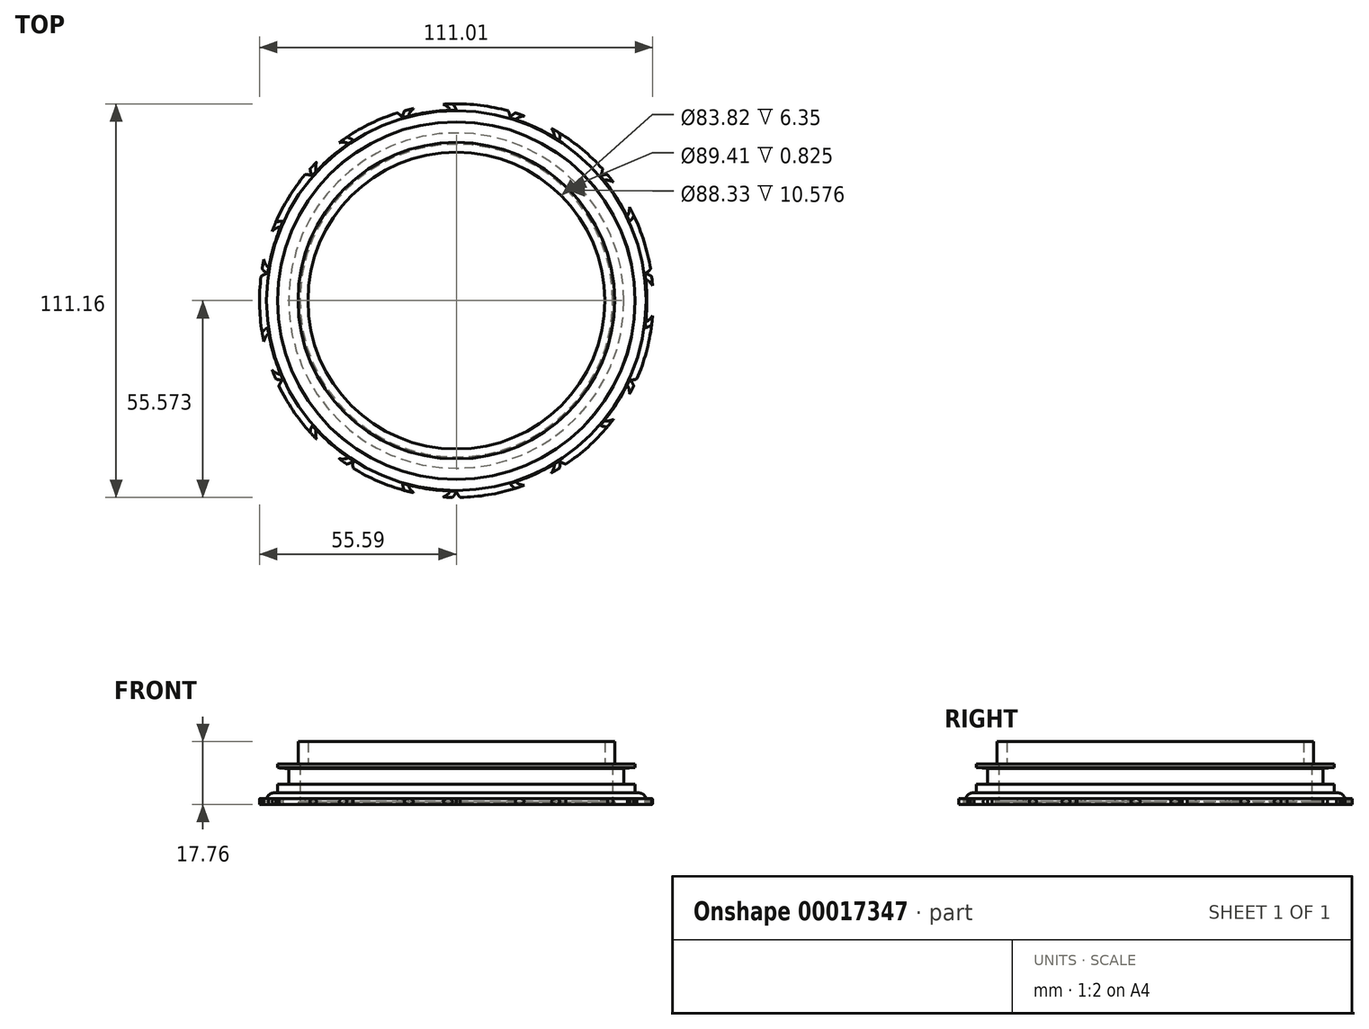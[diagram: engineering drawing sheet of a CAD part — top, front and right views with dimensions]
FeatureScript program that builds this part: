
annotation { "Feature Type Name" : "Feature", "Feature Type Description" : "" }
export const myFeature = defineFeature(function(context is Context, id is Id, definition is map)
    precondition{}
    {
        {
            var Q0;
            Q0=qCreatedBy(makeId("Top.planeOp"),FACE);
            var sketch = newSketch(context, id + "F0", { "sketchPlane" : qUnion([Q0])});
            skCircle(sketch, "E0", {"center": v(0, 0) * mm, "radius": 57.15 * mm, "construction": true});
            skLineSegment(sketch, "E1", {"start": v(0, 0) * mm, "end": v(0, 57.15) * mm, "construction": true});
            skCircle(sketch, "E2", {"center": v(0, 3.34) * mm, "radius": 53.8 * mm});
            skCircle(sketch, "E3", {"center": v(0, 3.34) * mm, "radius": 3.34 * mm, "construction": true});
            skLineSegment(sketch, "E4", {"start": v(0, 3.34) * mm, "end": v(-29.1, 48.6) * mm, "construction": true});
            skLineSegment(sketch, "E5", {"start": v(0, 57.15) * mm, "end": v(-29.1, 48.6) * mm, "construction": true});
            skLineSegment(sketch, "E6", {"start": v(-14.55, 52.88) * mm, "end": v(-29.1, 48.6) * mm, "construction": true});
            skLineSegment(sketch, "E7", {"start": v(-14.02, 24.18) * mm, "end": v(-21.82, 50.74) * mm, "construction": true});
            skCircle(sketch, "E8", {"center": v(-14.55, 52.88) * mm, "radius": 7.58 * mm, "construction": true});
            skLineSegment(sketch, "E9", {"start": v(-15.16, 54.97) * mm, "end": v(-16.68, 60.15) * mm, "construction": true});
            skEllipticalArc(sketch, "E10", {});
            skPoint(sketch, "E11", {"position": v(-15.16, 54.97) * mm});
            skLineSegment(sketch, "E12", {"start": v(-15.16, 54.97) * mm, "end": v(0, 54.97) * mm, "construction": true});
            skPoint(sketch, "E13", {"position": v(-7.58, 54.97) * mm});
            skCircle(sketch, "E14", {"center": v(0, 54.97) * mm, "radius": 7.58 * mm, "construction": true});
            skPoint(sketch, "E15", {"position": v(0, 62.55) * mm});
            skEllipticalArc(sketch, "E16", {});
            skCircle(sketch, "E17", {"center": v(0, 3.34) * mm, "radius": 44.7 * mm});
            skEllipticalArc(sketch, "E18.trimOffspring", {});
            skEllipticalArc(sketch, "E19.trimOffspring", {});
            skLineSegment(sketch, "E20", {"start": v(0, 3.34) * mm, "end": v(-8.33, 61.3) * mm, "construction": true});
            skCircle(sketch, "E21", {"center": v(0, 3.34) * mm, "radius": 55.59 * mm});
            skCircle(sketch, "E22", {"center": v(0, 3.34) * mm, "radius": 127 * mm});
            skLineSegment(sketch, "E23", {"start": v(0, 3.34) * mm, "end": v(-127, 3.34) * mm, "construction": true});
            skLineSegment(sketch, "E24", {"start": v(-53.8, 3.34) * mm, "end": v(-55.59, 3.34) * mm, "construction": true});
            skFitSpline(sketch, "E25.0", {"points": [v(-14.18, 56.14) * mm, v(-14.4, 54.97) * mm, v(-14.18, 53.8) * mm, v(-13.58, 52.8) * mm, v(-12.83, 52) * mm, v(-11.9, 51.22) * mm, v(-10.42, 50.32) * mm, v(-8.6, 49.57) * mm, v(-6.94, 49.07) * mm, v(-5.2, 48.66) * mm, v(-3.36, 48.38) * mm, v(-1.45, 48.24) * mm, v(0, 48.2) * mm, v(1.45, 48.24) * mm, v(3.36, 48.38) * mm, v(5.2, 48.66) * mm, v(6.94, 49.07) * mm, v(8.6, 49.57) * mm, v(10.42, 50.32) * mm, v(11.9, 51.22) * mm, v(12.83, 52) * mm, v(13.58, 52.8) * mm, v(14.18, 53.8) * mm, v(14.4, 54.97) * mm, v(14.18, 56.14) * mm, v(13.58, 57.14) * mm, v(12.83, 57.94) * mm, v(11.9, 58.72) * mm, v(10.42, 59.62) * mm, v(8.6, 60.37) * mm, v(6.94, 60.87) * mm, v(5.2, 61.28) * mm, v(3.36, 61.56) * mm, v(1.45, 61.7) * mm, v(0, 61.74) * mm, v(-1.45, 61.7) * mm, v(-3.36, 61.56) * mm, v(-5.2, 61.28) * mm, v(-6.94, 60.87) * mm, v(-8.6, 60.37) * mm, v(-10.42, 59.62) * mm, v(-11.9, 58.72) * mm, v(-12.83, 57.94) * mm, v(-13.58, 57.14) * mm, v(-14.18, 56.14) * mm, v(-14.4, 54.97) * mm, v(-14.18, 53.8) * mm]});
            skFitSpline(sketch, "E25.1", {"points": [v(-0.6, 55.75) * mm, v(-0.72, 56.94) * mm, v(-1.27, 58) * mm, v(-2.13, 58.8) * mm, v(-3.07, 59.34) * mm, v(-4.19, 59.83) * mm, v(-5.86, 60.28) * mm, v(-7.82, 60.48) * mm, v(-9.55, 60.5) * mm, v(-11.33, 60.4) * mm, v(-13.18, 60.15) * mm, v(-15.05, 59.75) * mm, v(-16.45, 59.37) * mm, v(-17.84, 58.93) * mm, v(-19.63, 58.25) * mm, v(-21.32, 57.47) * mm, v(-22.87, 56.58) * mm, v(-24.31, 55.64) * mm, v(-25.85, 54.4) * mm, v(-27.02, 53.13) * mm, v(-27.7, 52.12) * mm, v(-28.19, 51.14) * mm, v(-28.48, 50) * mm, v(-28.37, 48.82) * mm, v(-27.82, 47.76) * mm, v(-26.96, 46.97) * mm, v(-26.02, 46.41) * mm, v(-24.9, 45.93) * mm, v(-23.23, 45.48) * mm, v(-21.27, 45.27) * mm, v(-19.54, 45.26) * mm, v(-17.76, 45.36) * mm, v(-15.91, 45.61) * mm, v(-14.04, 46.01) * mm, v(-12.64, 46.39) * mm, v(-11.25, 46.83) * mm, v(-9.47, 47.5) * mm, v(-7.77, 48.3) * mm, v(-6.22, 49.18) * mm, v(-4.78, 50.11) * mm, v(-3.24, 51.35) * mm, v(-2.08, 52.63) * mm, v(-1.4, 53.64) * mm, v(-0.9, 54.62) * mm, v(-0.6, 55.75) * mm, v(-0.72, 56.94) * mm, v(-1.27, 58) * mm]});
            skLineSegment(sketch, "E26", {"start": v(0, 57.15) * mm, "end": v(0, 62.7) * mm, "construction": true});
            skPoint(sketch, "E27", {"position": v(0, 57.15) * mm});
            skArc(sketch, "E28", {"start": v(0, 57.15) * mm, "mid": v(-15.16, 54.97) * mm, "end": v(-29.1, 48.6) * mm});
            skArc(sketch, "E29", {"start": v(0, 57.15) * mm, "mid": v(-15.16, 54.97) * mm, "end": v(-29.1, 48.6) * mm, "construction": true});
            skCircle(sketch, "E30", {"center": v(0, 3.34) * mm, "radius": 41.91 * mm});
            const initialGuessF0  = {"E10": [-0.01454519881923172, 0.052879154308840354, 0.9594931524201487, 0.2817319478845903, 0.015159252343327363, 0.007579626171663686, 0, 0.9887715007810821], "E16": [0, 0.05497043346980581, -1, 0, 0.015159252343327398, 0.007579626171663695, 1.5707963267948966, 4.71238898038469], "E18.trimOffspring": [0, 0.05497043346980581, -1, 0, 0.015159252343327398, 0.007579626171663695, 5.294413806398706, 0], "E19.trimOffspring": [-0.014545198819231721, 0.05287915430884035, 0.9594931524201485, 0.2817319478845903, 0.015159252343327363, 0.007579626171663686, 1.5707963267948968, 3.141592653589793]};
            skSetInitialGuess(sketch, initialGuessF0);
            skSolve(sketch);
        }
        {
            var Q0;
            Q0=sQuery(id+"F0.wireOp",VERTEX,"E10.start");
            var Q1;
            Q1=sQuery(id+"F0.wireOp",EDGE,"E1");
            cPlane(context, id + "F1", {"entities" : qUnion([Q0, Q1]), "cplaneType" : CPlaneType.LINE_POINT, "offset" : 152.4 * mm, "width" : 152.4 * mm, "height" : 152.4 * mm});
        }
        {
            var Q0;
            Q0=qCreatedBy(id+"F1.planeOp",FACE);
            var sketch = newSketch(context, id + "F2", { "sketchPlane" : qUnion([Q0])});
            skCircle(sketch, "E31", {"center": v(0.82, 0.03) * mm, "radius": 0.83 * mm});
            skPoint(sketch, "E31.first.point", {"position": v(0, 0) * mm});
            skPoint(sketch, "E31.second.point", {"position": v(1.64, 0.15) * mm});
            skPoint(sketch, "E31.third.point", {"position": v(0.7, 0.85) * mm});
            skLineSegment(sketch, "E32", {"start": v(0, 0) * mm, "end": v(23.51, 0.85) * mm, "construction": true});
            skSolve(sketch);
        }
        {
            var Q0;
            Q0=qSketchRegion(id+"F2",true);
            var Q1;
            Q1=sQuery(id+"F0.wireOp",EDGE,"E10");
            sweep(context, id + "F3", {"profiles" : qUnion([Q0]), "path" : qUnion([Q1])});
        }
        {
            var Q0;
            Q0=sQuery(id+"F0.wireOp",EDGE,"E20");
            cPlane(context, id + "F4", {"entities" : qUnion([Q0]), "cplaneType" : CPlaneType.LINE_ANGLE, "offset" : 152.4 * mm, "angle" : 90 * degree, "width" : 152.4 * mm, "height" : 152.4 * mm});
        }
        {
            var Q0;
            Q0=qCreatedBy(makeId("Right.planeOp"),FACE);
            var sketch = newSketch(context, id + "F5", { "sketchPlane" : qUnion([Q0])});
            skLineSegment(sketch, "E33", {"start": v(3.34, 0) * mm, "end": v(3.34, 43.32) * mm, "construction": true});
            skSolve(sketch);
        }
        {
            var Q0;
            Q0=makeQuery(id+"F3.opSweep","SWEPT_BODY",BODY,{"disambiguationData":[OSD([sQuery(id+"F0.wireOp",EDGE,"E10"),sQuery(id+"F2.wireOp",EDGE,"E31")])]});
            var Q1;
            Q1=qCreatedBy(id+"F4.planeOp",FACE);
            mirror(context, id + "F6", {"operationType" : NewBodyOperationType.ADD, "entities" : qUnion([Q0]), "mirrorPlane" : qUnion([Q1])});
        }
        {
            var Q0;
            {var subQ3=sQuery(id+"F0.wireOp",EDGE,"E2");var subQ5=sQuery(id+"F0.wireOp",EDGE,"E25.1");var subQ7=makeQuery(id+"F0.imprint","INTERSECT",VERTEX,{"derivedFrom":[subQ3,subQ5]});Q0=makeQuery(id+"F0.imprint","IMPRINT",FACE,{"disambiguationData":[TD([[makeQuery(id+"F0.imprint","IMPRINT",EDGE,{"disambiguationData":[TD([[subQ7,-1.0]])],"derivedFrom":subQ3}),-1.0]])]});}
            extrude(context, id + "F7", {"entities" : qUnion([Q0]), "operationType" : NewBodyOperationType.ADD, "endBound" : BoundingType.SYMMETRIC, "depth" : 1.65 * mm});
        }
        {
            var Q0;
            Q0=makeQuery(id+"F3.opSweep","SWEPT_BODY",BODY,{"disambiguationData":[OSD([sQuery(id+"F0.wireOp",EDGE,"E10"),sQuery(id+"F2.wireOp",EDGE,"E31")])]});
            var Q1;
            Q1=sQuery(id+"F5.wireOp",EDGE,"E33");
            circularPattern(context, id + "F8", {"entities" : qUnion([Q0]), "axis" : qUnion([Q1]), "angle" : 32.73 * degree, "instanceCount" : round(11)});
        }
        {
            var Q0;
            Q0=makeQuery(id+"F0.imprint","IMPRINT",FACE,{"disambiguationData":[TD([[makeQuery(id+"F0.imprint","IMPRINT",EDGE,{"derivedFrom":sQuery(id+"F0.wireOp",EDGE,"E17")}),-1.0]])]});
            extrude(context, id + "F9", {"entities" : qUnion([Q0]), "operationType" : NewBodyOperationType.ADD, "endBound" : BoundingType.SYMMETRIC, "depth" : 1.65 * mm});
        }
        {
            var Q0;
            Q0=makeQuery(id+"F0.imprint","IMPRINT",FACE,{"disambiguationData":[TD([[makeQuery(id+"F0.imprint","IMPRINT",EDGE,{"derivedFrom":sQuery(id+"F0.wireOp",EDGE,"E22")}),1.0]])]});
            var Q1;
            {var subQ6=sQuery(id+"F0.wireOp",EDGE,"E18.trimOffspring");var subQ8=sQuery(id+"F0.wireOp",EDGE,"E10");var subQ10=makeQuery(id+"F0.imprint","INTERSECT",VERTEX,{"derivedFrom":[subQ8,subQ6]});Q1=makeQuery(id+"F0.imprint","IMPRINT",FACE,{"disambiguationData":[TD([[makeQuery(id+"F0.imprint","IMPRINT",EDGE,{"disambiguationData":[TD([[subQ10,1.0]])],"derivedFrom":subQ8}),1.0]])]});}
            var Q2;
            {var subQ0=sQuery(id+"F0.wireOp",EDGE,"E25.1");var subQ1=sQuery(id+"F0.wireOp",EDGE,"E21");var subQ2=makeQuery(id+"F0.imprint","INTERSECT",VERTEX,{"derivedFrom":[subQ1,subQ0]});Q2=makeQuery(id+"F0.imprint","IMPRINT",FACE,{"disambiguationData":[TD([[makeQuery(id+"F0.imprint","IMPRINT",EDGE,{"disambiguationData":[TD([[subQ2,-1.0]])],"derivedFrom":subQ1}),-1.0]])]});}
            extrude(context, id + "F10", {"entities" : qUnion([Q0, Q1, Q2]), "operationType" : NewBodyOperationType.REMOVE, "endBound" : BoundingType.SYMMETRIC, "oppositeDirection" : true, "depth" : 25.4 * mm});
        }
        {
            var Q0;
            Q0=qCreatedBy(makeId("Right.planeOp"),FACE);
            var sketch = newSketch(context, id + "F11", { "sketchPlane" : qUnion([Q0])});
            skLineSegment(sketch, "E34", {"start": v(-50.36, 0) * mm, "end": v(-50.36, 0.2) * mm});
            skLineSegment(sketch, "E35", {"start": v(-48.07, 2.48) * mm, "end": v(-47.18, 2.48) * mm});
            skLineSegment(sketch, "E36", {"start": v(-47.18, 2.48) * mm, "end": v(-47.18, 4.94) * mm});
            skLineSegment(sketch, "E37", {"start": v(-47.18, 4.94) * mm, "end": v(-44, 4.94) * mm});
            skLineSegment(sketch, "E38", {"start": v(-44, 4.94) * mm, "end": v(-44, 9.3) * mm});
            skLineSegment(sketch, "E39", {"start": v(-44, 9.3) * mm, "end": v(-47.17, 9.58) * mm});
            skLineSegment(sketch, "E40", {"start": v(-47.17, 9.58) * mm, "end": v(-47.17, 10.58) * mm});
            skLineSegment(sketch, "E41", {"start": v(-47.17, 10.58) * mm, "end": v(-40.82, 10.58) * mm});
            skLineSegment(sketch, "E42", {"start": v(-40.82, 10.58) * mm, "end": v(-40.82, 0) * mm});
            skLineSegment(sketch, "E43", {"start": v(-40.82, 0) * mm, "end": v(-50.36, 0) * mm});
            skPoint(sketch, "E44.visualSharp", {"position": v(-50.36, 2.48) * mm});
            skArc(sketch, "E44.filletArc", {"start": v(-48.07, 2.48) * mm, "mid": v(-49.69, 1.8) * mm, "end": v(-50.36, 0.2) * mm});
            skLineSegment(sketch, "E45", {"start": v(-44, 9.3) * mm, "end": v(-48.41, 9.3) * mm, "construction": true});
            skLineSegment(sketch, "E46", {"start": v(-48.41, 9.3) * mm, "end": v(-51.55, 9.3) * mm, "construction": true});
            skSolve(sketch);
        }
        {
            var Q0;
            Q0=makeQuery(id+"F11.imprint","IMPRINT",FACE,{"disambiguationData":[TD([[makeQuery(id+"F11.imprint","IMPRINT",EDGE,{"derivedFrom":sQuery(id+"F11.wireOp",EDGE,"E34")}),-1.0]])]});
            var Q1;
            Q1=sQuery(id+"F5.wireOp",EDGE,"E33");
            revolve(context, id + "F12", {"operationType" : NewBodyOperationType.ADD, "entities" : qUnion([Q0]), "axis" : qUnion([Q1]), "revolveType" : RevolveType.FULL});
        }
        {
            var Q0;
            Q0=makeQuery(id+"F0.imprint","IMPRINT",FACE,{"disambiguationData":[TD([[makeQuery(id+"F0.imprint","IMPRINT",EDGE,{"derivedFrom":sQuery(id+"F0.wireOp",EDGE,"E17")}),1.0]])]});
            extrude(context, id + "F13", {"entities" : qUnion([Q0]), "depth" : 16.93 * mm, "hasSecondDirection" : true, "secondDirectionOppositeDirection" : false, "secondDirectionDepth" : 10.58 * mm});
        }
    });
